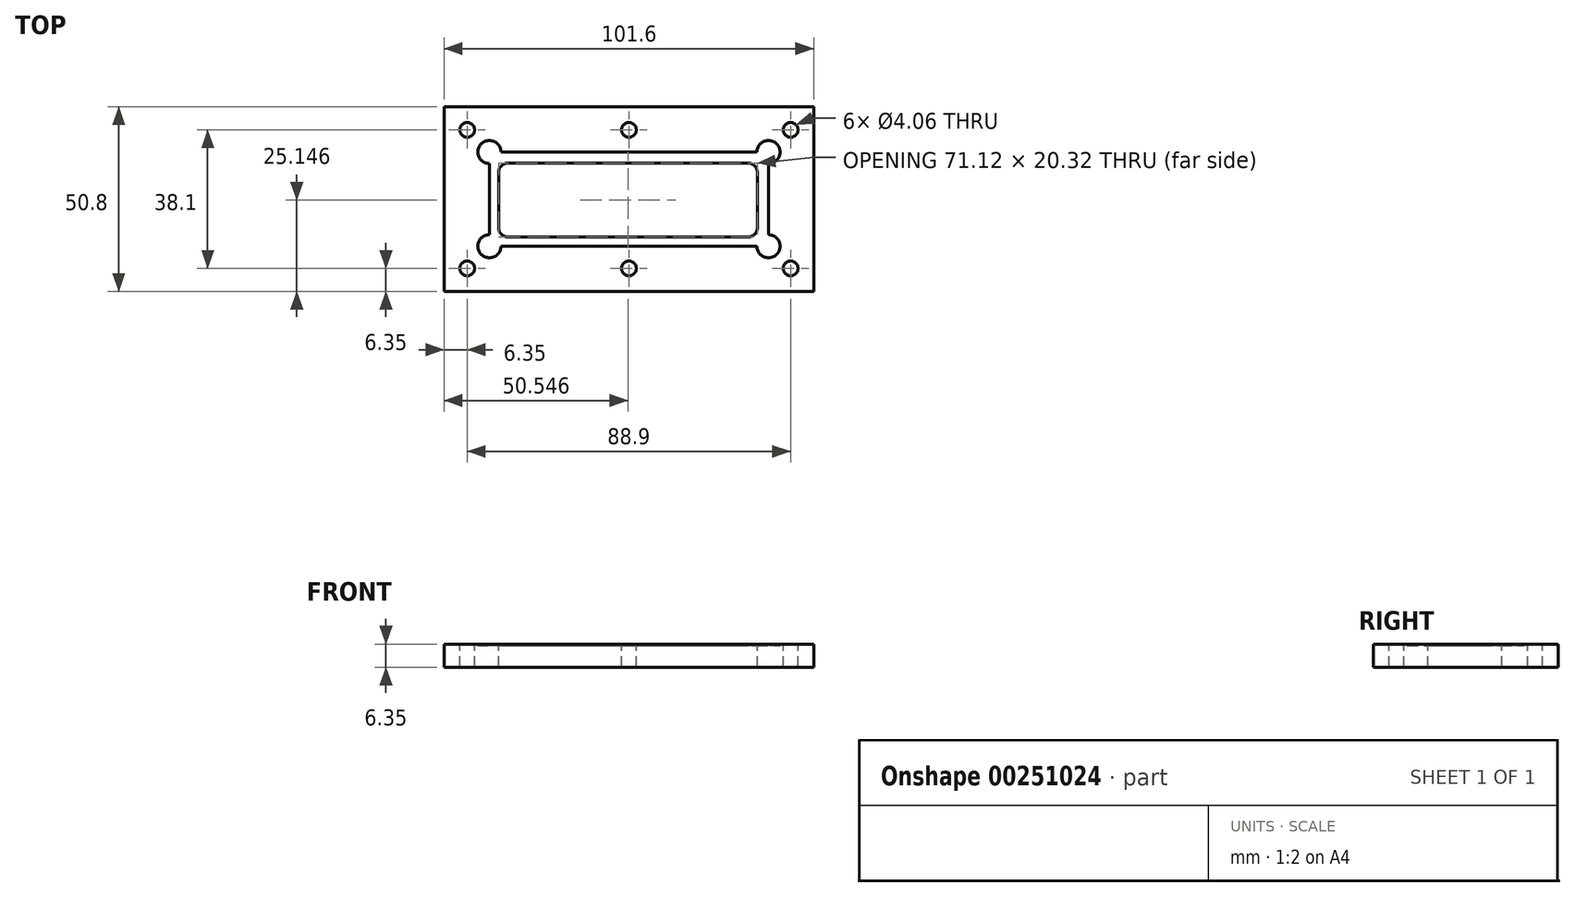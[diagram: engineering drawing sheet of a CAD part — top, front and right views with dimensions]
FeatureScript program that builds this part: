
annotation { "Feature Type Name" : "Feature", "Feature Type Description" : "" }
export const myFeature = defineFeature(function(context is Context, id is Id, definition is map)
    precondition{}
    {
        {
            var Q0;
            Q0=qCreatedBy(makeId("Top.planeOp"),FACE);
            var sketch = newSketch(context, id + "F0", { "sketchPlane" : qUnion([Q0])});
            skLineSegment(sketch, "E0.bottom", {"start": v(0, 0) * mm, "end": v(101.6, 0) * mm});
            skLineSegment(sketch, "E0.top", {"start": v(0, 50.8) * mm, "end": v(101.6, 50.8) * mm});
            skLineSegment(sketch, "E0.left", {"start": v(0, 0) * mm, "end": v(0, 50.8) * mm});
            skLineSegment(sketch, "E0.right", {"start": v(101.6, 0) * mm, "end": v(101.6, 50.8) * mm});
            skSolve(sketch);
        }
        {
            var Q0;
            Q0=makeQuery(id+"F0.imprint","IMPRINT",FACE,{"disambiguationData":[TD([[makeQuery(id+"F0.imprint","IMPRINT",EDGE,{"derivedFrom":sQuery(id+"F0.wireOp",EDGE,"E0.bottom")}),1.0]])]});
            extrude(context, id + "F1", {"entities" : qUnion([Q0]), "depth" : 6.35 * mm});
        }
        {
            var Q0;
            Q0=makeQuery(id+"F1.opExtrude","CAP_FACE",FACE,{"disambiguationData":[OSD([sQuery(id+"F0.wireOp",EDGE,"E0.bottom"),sQuery(id+"F0.wireOp",EDGE,"E0.top"),sQuery(id+"F0.wireOp",EDGE,"E0.left"),sQuery(id+"F0.wireOp",EDGE,"E0.right")])],"isStart":false});
            var sketch = newSketch(context, id + "F2", { "sketchPlane" : qUnion([Q0])});
            skLineSegment(sketch, "E1.bottom", {"start": v(12.45, 12.45) * mm, "end": v(89.15, 12.45) * mm});
            skLineSegment(sketch, "E1.top", {"start": v(12.45, 38.35) * mm, "end": v(89.15, 38.35) * mm});
            skLineSegment(sketch, "E1.left", {"start": v(12.45, 12.45) * mm, "end": v(12.45, 38.35) * mm});
            skLineSegment(sketch, "E1.right", {"start": v(89.15, 12.45) * mm, "end": v(89.15, 38.35) * mm});
            skCircle(sketch, "E2", {"center": v(12.45, 38.35) * mm, "radius": 3.18 * mm});
            skCircle(sketch, "E3", {"center": v(89.15, 38.35) * mm, "radius": 3.18 * mm});
            skCircle(sketch, "E4", {"center": v(89.15, 12.45) * mm, "radius": 3.18 * mm});
            skCircle(sketch, "E5", {"center": v(12.45, 12.45) * mm, "radius": 3.18 * mm});
            skSolve(sketch);
        }
        {
            var Q0;
            {var subQ0=sQuery(id+"F2.wireOp",EDGE,"E5");var subQ13=sQuery(id+"F2.wireOp",EDGE,"E1.bottom");var subQ15=makeQuery(id+"F2.imprint","INTERSECT",VERTEX,{"derivedFrom":[subQ13,subQ0]});Q0=makeQuery(id+"F2.imprint","IMPRINT",FACE,{"disambiguationData":[TD([[makeQuery(id+"F2.imprint","IMPRINT",EDGE,{"disambiguationData":[TD([[subQ15,-1.0]])],"derivedFrom":subQ13}),1.0]])]});}
            var Q1;
            {var subQ0=sQuery(id+"F2.wireOp",EDGE,"E1.right");var subQ1=sQuery(id+"F2.wireOp",EDGE,"E1.top");var subQ2=makeQuery(id+"F2.imprint","INTERSECT",VERTEX,{"derivedFrom":[subQ1,subQ0]});Q1=makeQuery(id+"F2.imprint","IMPRINT",FACE,{"disambiguationData":[TD([[makeQuery(id+"F2.imprint","IMPRINT",EDGE,{"disambiguationData":[TD([[subQ2,1.0]])],"derivedFrom":subQ1}),1.0]])]});}
            var Q2;
            {var subQ0=sQuery(id+"F2.wireOp",EDGE,"E1.right");var subQ1=sQuery(id+"F2.wireOp",EDGE,"E1.top");var subQ2=makeQuery(id+"F2.imprint","INTERSECT",VERTEX,{"derivedFrom":[subQ1,subQ0]});Q2=makeQuery(id+"F2.imprint","IMPRINT",FACE,{"disambiguationData":[TD([[makeQuery(id+"F2.imprint","IMPRINT",EDGE,{"disambiguationData":[TD([[subQ2,1.0]])],"derivedFrom":subQ1}),-1.0]])]});}
            var Q3;
            {var subQ0=sQuery(id+"F2.wireOp",EDGE,"E1.left");var subQ1=sQuery(id+"F2.wireOp",EDGE,"E1.top");var subQ2=makeQuery(id+"F2.imprint","INTERSECT",VERTEX,{"derivedFrom":[subQ1,subQ0]});Q3=makeQuery(id+"F2.imprint","IMPRINT",FACE,{"disambiguationData":[TD([[makeQuery(id+"F2.imprint","IMPRINT",EDGE,{"disambiguationData":[TD([[subQ2,-1.0]])],"derivedFrom":subQ1}),-1.0]])]});}
            var Q4;
            {var subQ0=sQuery(id+"F2.wireOp",EDGE,"E1.left");var subQ1=sQuery(id+"F2.wireOp",EDGE,"E1.top");var subQ2=makeQuery(id+"F2.imprint","INTERSECT",VERTEX,{"derivedFrom":[subQ1,subQ0]});Q4=makeQuery(id+"F2.imprint","IMPRINT",FACE,{"disambiguationData":[TD([[makeQuery(id+"F2.imprint","IMPRINT",EDGE,{"disambiguationData":[TD([[subQ2,-1.0]])],"derivedFrom":subQ1}),1.0]])]});}
            var Q5;
            {var subQ0=sQuery(id+"F2.wireOp",EDGE,"E1.right");var subQ1=sQuery(id+"F2.wireOp",EDGE,"E1.bottom");var subQ2=makeQuery(id+"F2.imprint","INTERSECT",VERTEX,{"derivedFrom":[subQ1,subQ0]});Q5=makeQuery(id+"F2.imprint","IMPRINT",FACE,{"disambiguationData":[TD([[makeQuery(id+"F2.imprint","IMPRINT",EDGE,{"disambiguationData":[TD([[subQ2,1.0]])],"derivedFrom":subQ1}),-1.0]])]});}
            var Q6;
            {var subQ0=sQuery(id+"F2.wireOp",EDGE,"E1.right");var subQ1=sQuery(id+"F2.wireOp",EDGE,"E1.bottom");var subQ2=makeQuery(id+"F2.imprint","INTERSECT",VERTEX,{"derivedFrom":[subQ1,subQ0]});Q6=makeQuery(id+"F2.imprint","IMPRINT",FACE,{"disambiguationData":[TD([[makeQuery(id+"F2.imprint","IMPRINT",EDGE,{"disambiguationData":[TD([[subQ2,1.0]])],"derivedFrom":subQ1}),1.0]])]});}
            var Q7;
            {var subQ0=sQuery(id+"F2.wireOp",EDGE,"E1.left");var subQ1=sQuery(id+"F2.wireOp",EDGE,"E1.bottom");var subQ2=makeQuery(id+"F2.imprint","INTERSECT",VERTEX,{"derivedFrom":[subQ1,subQ0]});Q7=makeQuery(id+"F2.imprint","IMPRINT",FACE,{"disambiguationData":[TD([[makeQuery(id+"F2.imprint","IMPRINT",EDGE,{"disambiguationData":[TD([[subQ2,-1.0]])],"derivedFrom":subQ1}),-1.0]])]});}
            var Q8;
            {var subQ0=sQuery(id+"F2.wireOp",EDGE,"E1.left");var subQ1=sQuery(id+"F2.wireOp",EDGE,"E1.bottom");var subQ2=makeQuery(id+"F2.imprint","INTERSECT",VERTEX,{"derivedFrom":[subQ1,subQ0]});Q8=makeQuery(id+"F2.imprint","IMPRINT",FACE,{"disambiguationData":[TD([[makeQuery(id+"F2.imprint","IMPRINT",EDGE,{"disambiguationData":[TD([[subQ2,-1.0]])],"derivedFrom":subQ1}),1.0]])]});}
            extrude(context, id + "F3", {"entities" : qUnion([Q0, Q1, Q2, Q3, Q4, Q5, Q6, Q7, Q8]), "operationType" : NewBodyOperationType.REMOVE, "oppositeDirection" : true, "depth" : 0.38 * mm});
        }
        {
            var Q0;
            Q0=makeQuery(id+"F3.boolean.opBoolean","COPY",FACE,{"derivedFrom":makeQuery(id+"F3.opExtrude","CAP_FACE",FACE,{"disambiguationData":[OSD([sQuery(id+"F2.wireOp",EDGE,"E1.bottom"),sQuery(id+"F2.wireOp",EDGE,"E1.top"),sQuery(id+"F2.wireOp",EDGE,"E1.left"),sQuery(id+"F2.wireOp",EDGE,"E1.right"),sQuery(id+"F2.wireOp",EDGE,"E2"),sQuery(id+"F2.wireOp",EDGE,"E3"),sQuery(id+"F2.wireOp",EDGE,"E4"),sQuery(id+"F2.wireOp",EDGE,"E5")])],"isStart":false})});
            var sketch = newSketch(context, id + "F4", { "sketchPlane" : qUnion([Q0])});
            skLineSegment(sketch, "E6.bottom", {"start": v(17.53, 14.99) * mm, "end": v(83.57, 14.99) * mm});
            skLineSegment(sketch, "E6.top", {"start": v(17.53, 35.3) * mm, "end": v(83.57, 35.3) * mm});
            skLineSegment(sketch, "E6.left", {"start": v(14.99, 17.53) * mm, "end": v(14.99, 32.77) * mm});
            skLineSegment(sketch, "E6.right", {"start": v(86.1, 17.53) * mm, "end": v(86.1, 32.77) * mm});
            skPoint(sketch, "E7.visualSharp", {"position": v(14.99, 35.3) * mm});
            skArc(sketch, "E7.filletArc", {"start": v(17.53, 35.3) * mm, "mid": v(15.73, 34.56) * mm, "end": v(14.99, 32.77) * mm});
            skPoint(sketch, "E8.visualSharp", {"position": v(14.99, 14.99) * mm});
            skArc(sketch, "E8.filletArc", {"start": v(14.99, 17.53) * mm, "mid": v(15.73, 15.73) * mm, "end": v(17.53, 14.99) * mm});
            skPoint(sketch, "E9.visualSharp", {"position": v(86.1, 14.99) * mm});
            skArc(sketch, "E9.filletArc", {"start": v(83.57, 14.99) * mm, "mid": v(85.36, 15.73) * mm, "end": v(86.1, 17.53) * mm});
            skPoint(sketch, "E10.visualSharp", {"position": v(86.1, 35.3) * mm});
            skArc(sketch, "E10.filletArc", {"start": v(86.1, 32.77) * mm, "mid": v(85.36, 34.56) * mm, "end": v(83.57, 35.3) * mm});
            skSolve(sketch);
        }
        {
            var Q0;
            Q0 = qSketchRegion(id + "F4", true);
            extrude(context, id + "F5", {"entities" : qUnion([Q0]), "operationType" : NewBodyOperationType.REMOVE, "endBound" : BoundingType.UP_TO_NEXT, "oppositeDirection" : true, "depth" : 25.4 * mm});
        }
        {
            var Q0;
            Q0=makeQuery(id+"F1.opExtrude","CAP_FACE",FACE,{"disambiguationData":[OSD([sQuery(id+"F0.wireOp",EDGE,"E0.bottom"),sQuery(id+"F0.wireOp",EDGE,"E0.top"),sQuery(id+"F0.wireOp",EDGE,"E0.left"),sQuery(id+"F0.wireOp",EDGE,"E0.right")])],"isStart":false});
            var sketch = newSketch(context, id + "F6", { "sketchPlane" : qUnion([Q0])});
            skCircle(sketch, "E11", {"center": v(6.35, 44.45) * mm, "radius": 2.03 * mm});
            skCircle(sketch, "E12", {"center": v(50.8, 44.45) * mm, "radius": 2.03 * mm});
            skCircle(sketch, "E13", {"center": v(95.25, 44.45) * mm, "radius": 2.03 * mm});
            skCircle(sketch, "E14", {"center": v(95.25, 6.35) * mm, "radius": 2.03 * mm});
            skCircle(sketch, "E15", {"center": v(50.8, 6.35) * mm, "radius": 2.03 * mm});
            skCircle(sketch, "E16", {"center": v(6.35, 6.35) * mm, "radius": 2.03 * mm});
            skSolve(sketch);
        }
        {
            var Q0;
            Q0 = qSketchRegion(id + "F6", true);
            extrude(context, id + "F7", {"entities" : qUnion([Q0]), "operationType" : NewBodyOperationType.REMOVE, "endBound" : BoundingType.UP_TO_NEXT, "oppositeDirection" : true, "depth" : 25.4 * mm});
        }
    });
